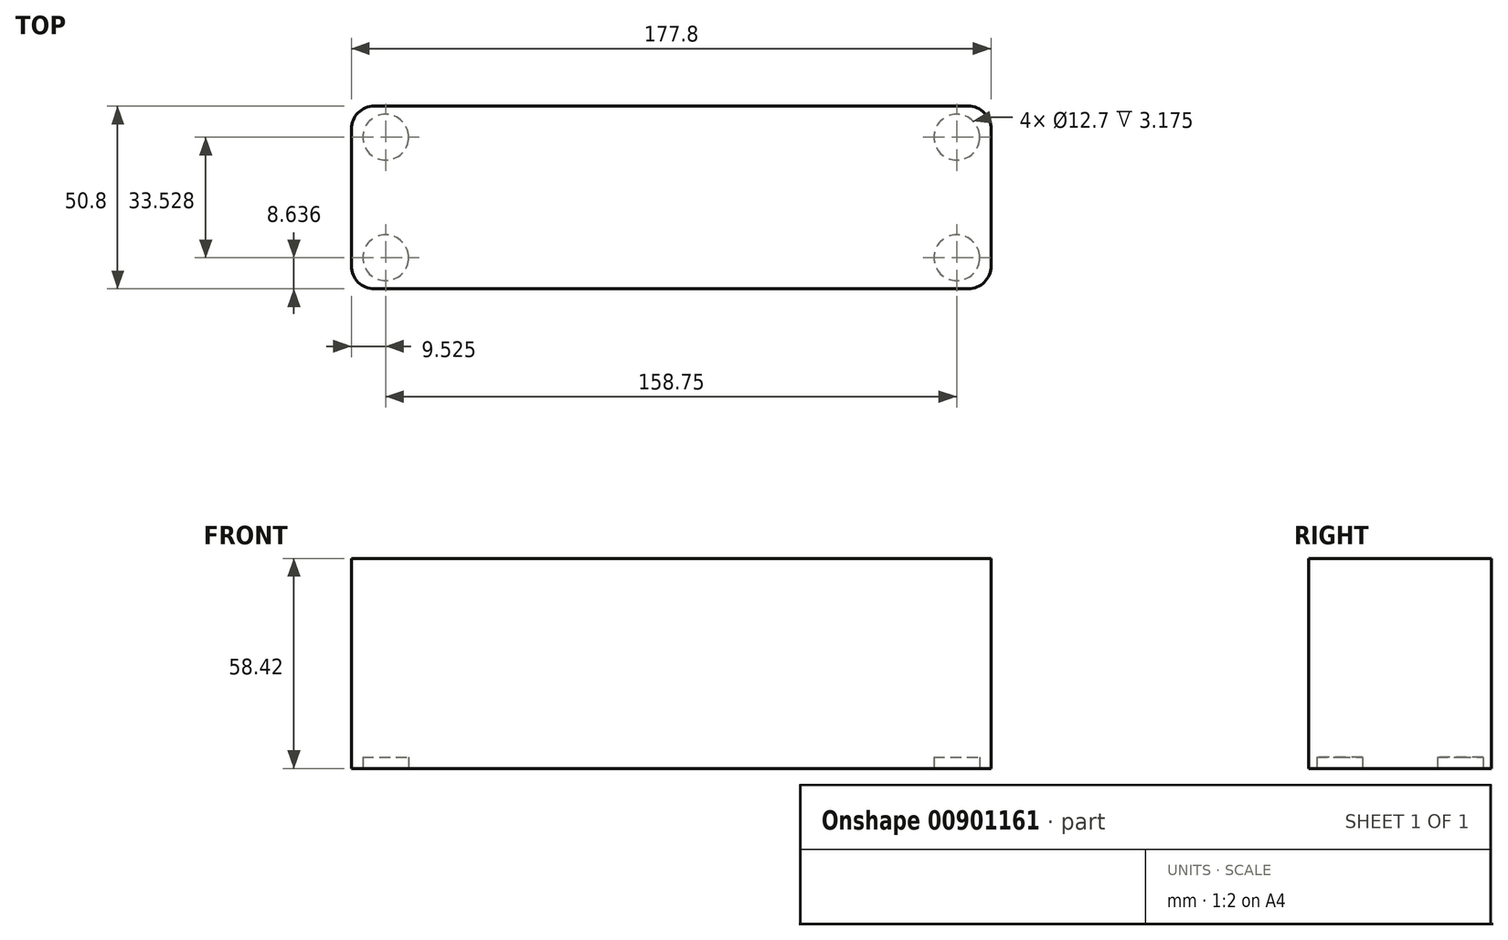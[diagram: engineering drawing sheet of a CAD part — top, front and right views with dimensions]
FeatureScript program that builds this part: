
annotation { "Feature Type Name" : "Feature", "Feature Type Description" : "" }
export const myFeature = defineFeature(function(context is Context, id is Id, definition is map)
    precondition{}
    {
        {
            var Q0;
            Q0=qCreatedBy(makeId("Top.planeOp"),FACE);
            var sketch = newSketch(context, id + "F0", { "sketchPlane" : qUnion([Q0])});
            skLineSegment(sketch, "E0.bottom", {"start": v(-88.9, 25.4) * mm, "end": v(88.9, 25.4) * mm});
            skLineSegment(sketch, "E0.top", {"start": v(-88.9, -25.4) * mm, "end": v(88.9, -25.4) * mm});
            skLineSegment(sketch, "E0.left", {"start": v(-88.9, 25.4) * mm, "end": v(-88.9, -25.4) * mm});
            skLineSegment(sketch, "E0.right", {"start": v(88.9, 25.4) * mm, "end": v(88.9, -25.4) * mm});
            skSolve(sketch);
        }
        {
            var Q0;
            Q0=makeQuery(id+"F0.imprint","IMPRINT",FACE,{"disambiguationData":[TD([[makeQuery(id+"F0.imprint","IMPRINT",EDGE,{"derivedFrom":sQuery(id+"F0.wireOp",EDGE,"E0.bottom")}),-1.0]])]});
            extrude(context, id + "F1", {"entities" : qUnion([Q0]), "depth" : 58.42 * mm, "offsetDistance" : 25.4 * mm});
        }
        {
            var Q0;
            Q0=makeQuery(id+"F1.opExtrude","SWEPT_EDGE",EDGE,{"disambiguationData":[OSD([sQuery(id+"F0.wireOp",EDGE,"E0.bottom"),sQuery(id+"F0.wireOp",EDGE,"E0.left")])]});
            var Q1;
            Q1=makeQuery(id+"F1.opExtrude","SWEPT_EDGE",EDGE,{"disambiguationData":[OSD([sQuery(id+"F0.wireOp",EDGE,"E0.bottom"),sQuery(id+"F0.wireOp",EDGE,"E0.right")])]});
            var Q2;
            Q2=makeQuery(id+"F1.opExtrude","SWEPT_EDGE",EDGE,{"disambiguationData":[OSD([sQuery(id+"F0.wireOp",EDGE,"E0.top"),sQuery(id+"F0.wireOp",EDGE,"E0.right")])]});
            var Q3;
            Q3=makeQuery(id+"F1.opExtrude","SWEPT_EDGE",EDGE,{"disambiguationData":[OSD([sQuery(id+"F0.wireOp",EDGE,"E0.top"),sQuery(id+"F0.wireOp",EDGE,"E0.left")])]});
            fillet(context, id + "F2", {"entities" : qUnion([Q0, Q1, Q2, Q3]), "radius" : 6.35 * mm, "tangentPropagation" : true, "allowEdgeOverflow" : false});
        }
        {
            var Q0;
            Q0=makeQuery(id+"F1.opExtrude","CAP_FACE",FACE,{"disambiguationData":[OSD([sQuery(id+"F0.wireOp",EDGE,"E0.bottom"),sQuery(id+"F0.wireOp",EDGE,"E0.top"),sQuery(id+"F0.wireOp",EDGE,"E0.left"),sQuery(id+"F0.wireOp",EDGE,"E0.right")])],"isStart":true});
            var sketch = newSketch(context, id + "F3", { "sketchPlane" : qUnion([Q0])});
            skCircle(sketch, "E1", {"center": v(79.38, 16.76) * mm, "radius": 6.35 * mm});
            skCircle(sketch, "E2.MirrorC", {"center": v(79.38, -16.76) * mm, "radius": 6.35 * mm});
            skCircle(sketch, "E3.MirrorC", {"center": v(-79.38, 16.76) * mm, "radius": 6.35 * mm});
            skCircle(sketch, "E4.MirrorC", {"center": v(-79.38, -16.76) * mm, "radius": 6.35 * mm});
            skSolve(sketch);
        }
        {
            var Q0;
            Q0 = qSketchRegion(id + "F3", true);
            extrude(context, id + "F4", {"entities" : qUnion([Q0]), "operationType" : NewBodyOperationType.REMOVE, "oppositeDirection" : true, "depth" : 3.17 * mm, "offsetDistance" : 25.4 * mm});
        }
    });
